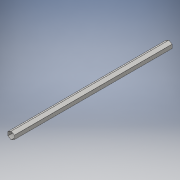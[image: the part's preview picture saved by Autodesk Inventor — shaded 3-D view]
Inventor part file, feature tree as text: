
AUTODESK INVENTOR PART (.ipt)
format: ipt  version: 2016 (Build 200138000, 138)  size: 114,176 bytes
history: native  units: mm
features: extrude x1, fillet x1, sketch x1
ambient origin geometry x8: Origin, YZ Plane, XZ Plane, XY Plane, X Axis, Y Axis, Z Axis, Center Point
bodies: Solid1 (feature_tree)
feature tree (3):
  extrude  "Extrusion1"  Depth=4.9mm
  fillet  "Fillet1"  Radius=120.0mm
  sketch  "Sketch1"  dims[d0=5.0mm d1=4.9mm d2=120.0mm d3=0.0mm d4=0.1mm]
